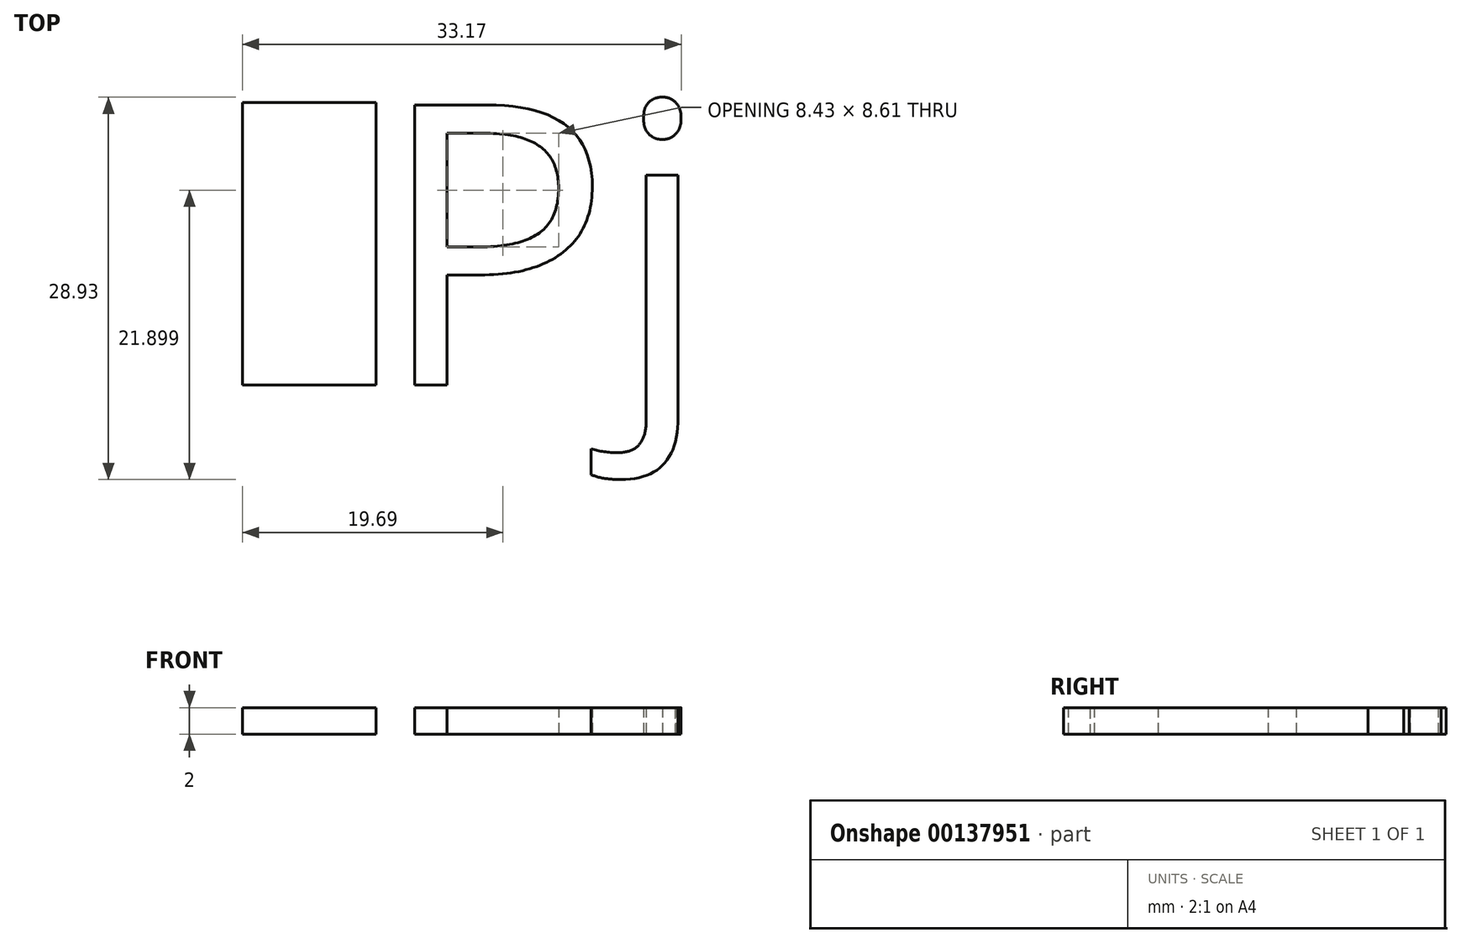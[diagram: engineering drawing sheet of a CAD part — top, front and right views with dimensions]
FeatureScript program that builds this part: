
annotation { "Feature Type Name" : "Feature", "Feature Type Description" : "" }
export const myFeature = defineFeature(function(context is Context, id is Id, definition is map)
    precondition{}
    {
        {
            var Q0;
            Q0=qCreatedBy(makeId("Top.planeOp"),FACE);
            var sketch = newSketch(context, id + "F0", { "sketchPlane" : qUnion([Q0])});
            skText(sketch, "E0", { "text": "Pj", "fontName": "OpenSans-Regular.ttf"});
            skLineSegment(sketch, "E1.bottom", {"start": v(0, 0) * mm, "end": v(-10.1, 0) * mm});
            skLineSegment(sketch, "E1.top", {"start": v(0, 21.38) * mm, "end": v(-10.1, 21.38) * mm});
            skLineSegment(sketch, "E1.left", {"start": v(0, 0) * mm, "end": v(0, 21.38) * mm});
            skLineSegment(sketch, "E1.right", {"start": v(-10.1, 0) * mm, "end": v(-10.1, 21.38) * mm});
            const initialGuessF0  = {"E0": [0, 0, 1, 0, 0.02138]};
            skSetInitialGuess(sketch, initialGuessF0);
            skSolve(sketch);
        }
        {
            var Q0;
            Q0 = qSketchRegion(id + "F0", true);
            extrude(context, id + "F1", {"entities" : qUnion([Q0]), "depth" : 2 * mm});
        }
    });
